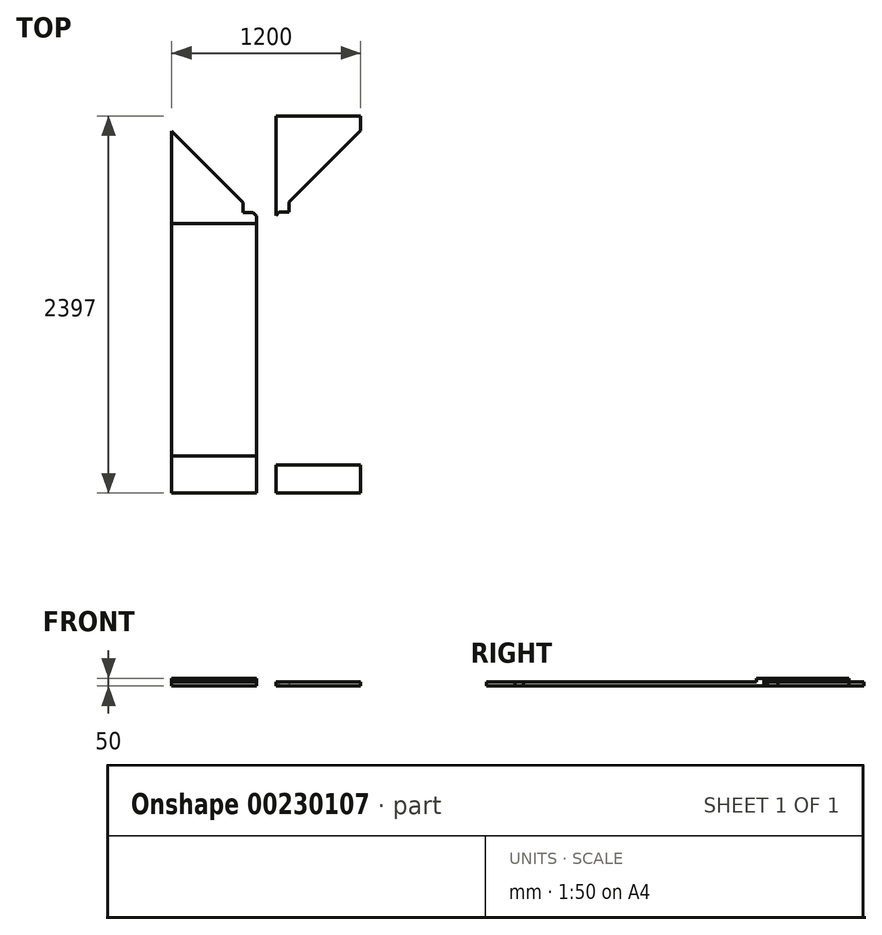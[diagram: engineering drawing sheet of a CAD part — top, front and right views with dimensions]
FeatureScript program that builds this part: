
annotation { "Feature Type Name" : "Feature", "Feature Type Description" : "" }
export const myFeature = defineFeature(function(context is Context, id is Id, definition is map)
    precondition{}
    {
        {
            var Q0;
            Q0=qCreatedBy(makeId("Top.planeOp"),FACE);
            var sketch = newSketch(context, id + "F0", { "sketchPlane" : qUnion([Q0])});
            skLineSegment(sketch, "E0.bottom", {"start": v(0, 2397) * mm, "end": v(1200, 2397) * mm});
            skLineSegment(sketch, "E1", {"start": v(1200, 2397) * mm, "end": v(1200, -3) * mm});
            skLineSegment(sketch, "E2", {"start": v(0, 2397) * mm, "end": v(0, 0) * mm});
            skLineSegment(sketch, "E3", {"start": v(0, 0) * mm, "end": v(1200, 0) * mm});
            skLineSegment(sketch, "E4.0", {"start": v(1200, 2303) * mm, "end": v(1200, 0) * mm});
            skLineSegment(sketch, "E5.0", {"start": v(662, 0) * mm, "end": v(1200, 0) * mm});
            skLineSegment(sketch, "E6.0", {"start": v(662, 1765) * mm, "end": v(662, 0) * mm});
            skLineSegment(sketch, "E7.0", {"start": v(662, 1708) * mm, "end": v(1200, 1708) * mm});
            skLineSegment(sketch, "E8.0", {"start": v(662, 180) * mm, "end": v(1200, 180) * mm});
            skLineSegment(sketch, "E9.0", {"start": v(682, 1785) * mm, "end": v(747, 1785) * mm});
            skLineSegment(sketch, "E10.0", {"start": v(747, 1785) * mm, "end": v(747, 1850) * mm});
            skLineSegment(sketch, "E11", {"start": v(662, 1765) * mm, "end": v(682, 1785) * mm});
            skLineSegment(sketch, "E12", {"start": v(747, 1850) * mm, "end": v(1200, 2303) * mm});
            skLineSegment(sketch, "E13", {"start": v(1100, 1708) * mm, "end": v(1100, 180) * mm});
            skLineSegment(sketch, "E14.bottom", {"start": v(1100, 1708) * mm, "end": v(1200, 1708) * mm});
            skLineSegment(sketch, "E14.top", {"start": v(1100, 180) * mm, "end": v(1200, 180) * mm});
            skLineSegment(sketch, "E14.right", {"start": v(1200, 1708) * mm, "end": v(1200, 180) * mm});
            skLineSegment(sketch, "E15.bottom", {"start": v(1100, 180) * mm, "end": v(662, 180) * mm});
            skLineSegment(sketch, "E15.top", {"start": v(1100, 1708) * mm, "end": v(662, 1708) * mm});
            skLineSegment(sketch, "E15.left", {"start": v(1100, 180) * mm, "end": v(1100, 1708) * mm});
            skLineSegment(sketch, "E15.right", {"start": v(662, 180) * mm, "end": v(662, 1708) * mm});
            skLineSegment(sketch, "E16.0", {"start": v(0, 0) * mm, "end": v(0, 2300) * mm});
            skLineSegment(sketch, "E17.0", {"start": v(538, 0) * mm, "end": v(538, 1762) * mm});
            skLineSegment(sketch, "E18.0", {"start": v(0, 0) * mm, "end": v(538, 0) * mm});
            skLineSegment(sketch, "E19.0", {"start": v(453, 1782) * mm, "end": v(453, 1847) * mm});
            skLineSegment(sketch, "E20.0", {"start": v(518, 1782) * mm, "end": v(453, 1782) * mm});
            skLineSegment(sketch, "E21", {"start": v(538, 1762) * mm, "end": v(518, 1782) * mm});
            skLineSegment(sketch, "E22", {"start": v(453, 1847) * mm, "end": v(0, 2300) * mm});
            skLineSegment(sketch, "E23", {"start": v(100, 1713) * mm, "end": v(100, 235) * mm});
            skLineSegment(sketch, "E24", {"start": v(0, 1713) * mm, "end": v(538, 1713) * mm});
            skLineSegment(sketch, "E25", {"start": v(0, 235) * mm, "end": v(538, 235) * mm});
            skLineSegment(sketch, "E26", {"start": v(538, 1762) * mm, "end": v(538, 2397) * mm});
            skLineSegment(sketch, "E27", {"start": v(662, 1765) * mm, "end": v(662, 2397) * mm});
            skSolve(sketch);
        }
        {
            var Q0;
            {var subQ5=sQuery(id+"F0.wireOp",EDGE,"E23");Q0=makeQuery(id+"F0.imprint","IMPRINT",FACE,{"disambiguationData":[TD([[makeQuery(id+"F0.imprint","IMPRINT",EDGE,{"derivedFrom":subQ5}),1.0]])]});}
            var Q1;
            Q1=makeQuery(id+"F0.imprint","IMPRINT",FACE,{"disambiguationData":[TD([[makeQuery(id+"F0.imprint","IMPRINT",EDGE,{"derivedFrom":sQuery(id+"F0.wireOp",EDGE,"E15.bottom")}),-1.0]])]});
            extrude(context, id + "F1", {"entities" : qUnion([Q0, Q1]), "depth" : 25 * mm});
        }
        {
            var Q0;
            Q0=makeQuery(id+"F0.imprint","IMPRINT",FACE,{"disambiguationData":[TD([[makeQuery(id+"F0.imprint","IMPRINT",EDGE,{"derivedFrom":sQuery(id+"F0.wireOp",EDGE,"E9.0")}),-1.0]])]});
            var Q1;
            {var subQ2=sQuery(id+"F0.wireOp",EDGE,"E5.0");Q1=makeQuery(id+"F0.imprint","IMPRINT",FACE,{"disambiguationData":[TD([[makeQuery(id+"F0.imprint","IMPRINT",EDGE,{"derivedFrom":subQ2}),1.0]])]});}
            var Q2;
            {var subQ4=sQuery(id+"F0.wireOp",EDGE,"E18.0");Q2=makeQuery(id+"F0.imprint","IMPRINT",FACE,{"disambiguationData":[TD([[makeQuery(id+"F0.imprint","IMPRINT",EDGE,{"derivedFrom":subQ4}),1.0]])]});}
            var Q3;
            Q3=makeQuery(id+"F0.imprint","IMPRINT",FACE,{"disambiguationData":[TD([[makeQuery(id+"F0.imprint","IMPRINT",EDGE,{"derivedFrom":sQuery(id+"F0.wireOp",EDGE,"E19.0")}),1.0]])]});
            extrude(context, id + "F2", {"entities" : qUnion([Q0, Q1, Q2, Q3]), "depth" : 25 * mm});
        }
        {
            var Q0;
            {var subQ5=sQuery(id+"F0.wireOp",EDGE,"E23");Q0=makeQuery(id+"F0.imprint","IMPRINT",FACE,{"disambiguationData":[TD([[makeQuery(id+"F0.imprint","IMPRINT",EDGE,{"derivedFrom":subQ5}),-1.0]])]});}
            var Q1;
            Q1=makeQuery(id+"F0.imprint","IMPRINT",FACE,{"disambiguationData":[TD([[makeQuery(id+"F0.imprint","IMPRINT",EDGE,{"derivedFrom":sQuery(id+"F0.wireOp",EDGE,"E14.bottom")}),-1.0]])]});
            extrude(context, id + "F3", {"entities" : qUnion([Q0, Q1]), "depth" : 25 * mm});
        }
        {
            var Q0;
            Q0=makeQuery(id+"F0.imprint","IMPRINT",FACE,{"disambiguationData":[TD([[makeQuery(id+"F0.imprint","IMPRINT",EDGE,{"derivedFrom":sQuery(id+"F0.wireOp",EDGE,"E9.0")}),1.0]])]});
            var Q1;
            Q1=makeQuery(id+"F2.opExtrude","CAP_FACE",FACE,{"disambiguationData":[OSD([sQuery(id+"F0.wireOp",EDGE,"E16.0"),sQuery(id+"F0.wireOp",EDGE,"E17.0"),sQuery(id+"F0.wireOp",EDGE,"E19.0"),sQuery(id+"F0.wireOp",EDGE,"E20.0"),sQuery(id+"F0.wireOp",EDGE,"E21"),sQuery(id+"F0.wireOp",EDGE,"E22"),sQuery(id+"F0.wireOp",EDGE,"E24")])],"isStart":false});
            var Q2;
            {var subQ0=sQuery(id+"F0.wireOp",EDGE,"E2");Q2=makeQuery(id+"F0.imprint","IMPRINT",FACE,{"disambiguationData":[TD([[makeQuery(id+"F0.imprint","IMPRINT",EDGE,{"derivedFrom":subQ0}),1.0]])]});}
            extrude(context, id + "F4", {"entities" : qUnion([Q0, Q1, Q2]), "operationType" : NewBodyOperationType.ADD, "depth" : 25 * mm});
        }
        {
            var Q0;
            {var subQ3=sQuery(id+"F0.wireOp",EDGE,"E3");Q0=makeQuery(id+"F0.imprint","IMPRINT",FACE,{"disambiguationData":[TD([[makeQuery(id+"F0.imprint","IMPRINT",EDGE,{"derivedFrom":subQ3}),1.0]])]});}
            extrude(context, id + "F5", {"entities" : qUnion([Q0]), "depth" : 25 * mm});
        }
    });
